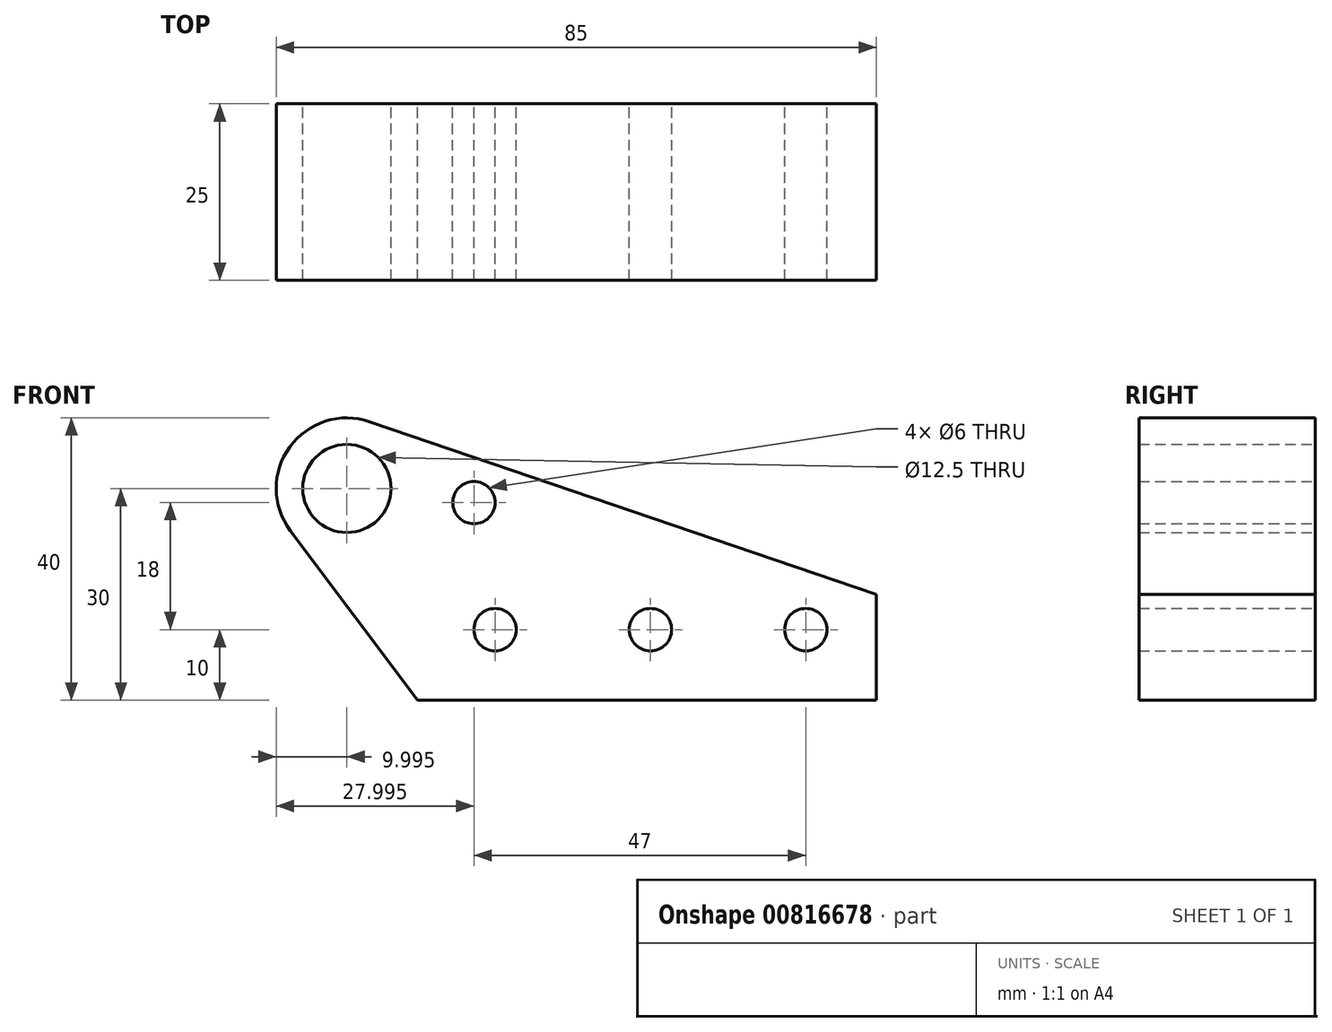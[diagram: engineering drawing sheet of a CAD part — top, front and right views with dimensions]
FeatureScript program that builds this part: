
annotation { "Feature Type Name" : "Feature", "Feature Type Description" : "" }
export const myFeature = defineFeature(function(context is Context, id is Id, definition is map)
    precondition{}
    {
        {
            var Q0;
            Q0=qCreatedBy(makeId("Front.planeOp"),FACE);
            var sketch = newSketch(context, id + "F0", { "sketchPlane" : qUnion([Q0])});
            skCircle(sketch, "E0", {"center": v(29.58, 10) * mm, "radius": 3 * mm});
            skLineSegment(sketch, "E1", {"start": v(39.58, 0) * mm, "end": v(-25.42, 0) * mm});
            skLineSegment(sketch, "E2", {"start": v(39.58, 0) * mm, "end": v(39.58, 15) * mm});
            skCircle(sketch, "E3", {"center": v(7.58, 10) * mm, "radius": 3 * mm});
            skCircle(sketch, "E4", {"center": v(-14.42, 10) * mm, "radius": 3 * mm});
            skCircle(sketch, "E5", {"center": v(-17.42, 28) * mm, "radius": 3 * mm});
            skCircle(sketch, "E6", {"center": v(-35.42, 30) * mm, "radius": 6.25 * mm});
            skArc(sketch, "E7", {"start": v(-32.2, 39.47) * mm, "mid": v(-43.52, 35.87) * mm, "end": v(-43.42, 24) * mm});
            skLineSegment(sketch, "E8", {"start": v(-25.42, 0) * mm, "end": v(-43.42, 24) * mm});
            skLineSegment(sketch, "E9", {"start": v(39.58, 15) * mm, "end": v(-32.2, 39.47) * mm});
            skSolve(sketch);
        }
        {
            var Q0;
            Q0 = qSketchRegion(id + "F0", true);
            extrude(context, id + "F1", {"entities" : qUnion([Q0]), "depth" : 25 * mm, "offsetDistance" : 25 * mm});
        }
    });
